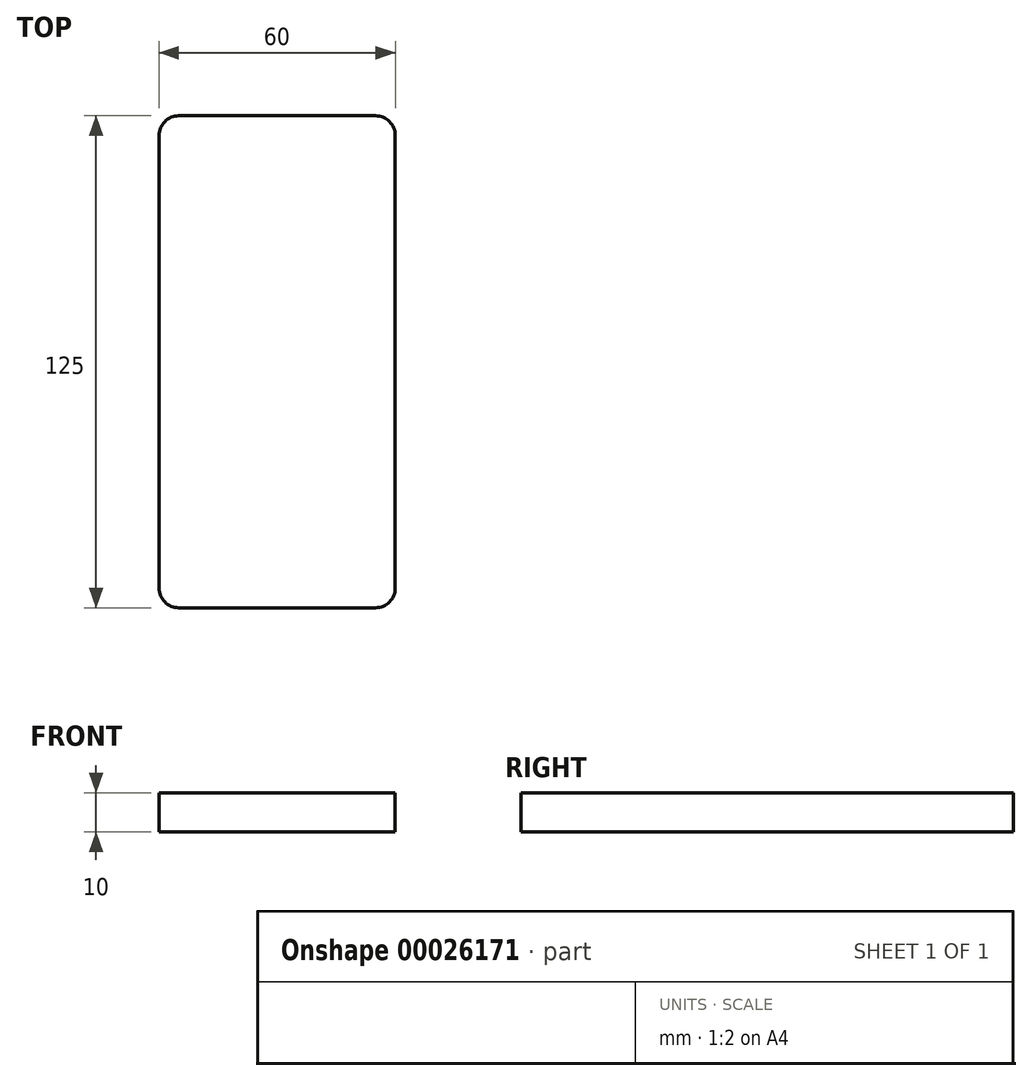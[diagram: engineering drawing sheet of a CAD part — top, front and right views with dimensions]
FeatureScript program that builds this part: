
annotation { "Feature Type Name" : "Feature", "Feature Type Description" : "" }
export const myFeature = defineFeature(function(context is Context, id is Id, definition is map)
    precondition{}
    {
        {
            var Q0;
            Q0=qCreatedBy(makeId("Top.planeOp"),FACE);
            var sketch = newSketch(context, id + "F0", { "sketchPlane" : qUnion([Q0])});
            skLineSegment(sketch, "E0.bottom", {"start": v(-32.55, -27.58) * mm, "end": v(27.45, -27.58) * mm});
            skLineSegment(sketch, "E0.top", {"start": v(-32.55, 97.42) * mm, "end": v(27.45, 97.42) * mm});
            skLineSegment(sketch, "E0.left", {"start": v(-32.55, -27.58) * mm, "end": v(-32.55, 97.42) * mm});
            skLineSegment(sketch, "E0.right", {"start": v(27.45, -27.58) * mm, "end": v(27.45, 97.42) * mm});
            skSolve(sketch);
        }
        {
            var Q0;
            Q0=makeQuery(id+"F0.imprint","IMPRINT",FACE,{"disambiguationData":[TD([[makeQuery(id+"F0.imprint","IMPRINT",EDGE,{"derivedFrom":sQuery(id+"F0.wireOp",EDGE,"E0.bottom")}),1.0]])]});
            extrude(context, id + "F1", {"entities" : qUnion([Q0]), "depth" : 10 * mm});
        }
        {
            var Q0;
            Q0=makeQuery(id+"F1.opExtrude","SWEPT_EDGE",EDGE,{"disambiguationData":[OSD([sQuery(id+"F0.wireOp",EDGE,"E0.bottom"),sQuery(id+"F0.wireOp",EDGE,"E0.left")])]});
            var Q1;
            Q1=makeQuery(id+"F1.opExtrude","SWEPT_EDGE",EDGE,{"disambiguationData":[OSD([sQuery(id+"F0.wireOp",EDGE,"E0.top"),sQuery(id+"F0.wireOp",EDGE,"E0.left")])]});
            var Q2;
            Q2=makeQuery(id+"F1.opExtrude","SWEPT_EDGE",EDGE,{"disambiguationData":[OSD([sQuery(id+"F0.wireOp",EDGE,"E0.top"),sQuery(id+"F0.wireOp",EDGE,"E0.right")])]});
            fillet(context, id + "F2", {"entities" : qUnion([Q0, Q1, Q2]), "radius" : 5 * mm, "tangentPropagation" : true, "allowEdgeOverflow" : false});
        }
        {
            var Q0;
            Q0=makeQuery(id+"F1.opExtrude","SWEPT_EDGE",EDGE,{"disambiguationData":[OSD([sQuery(id+"F0.wireOp",EDGE,"E0.bottom"),sQuery(id+"F0.wireOp",EDGE,"E0.right")])]});
            fillet(context, id + "F3", {"entities" : qUnion([Q0]), "radius" : 5 * mm, "tangentPropagation" : true, "allowEdgeOverflow" : false});
        }
        {
            var Q0;
            Q0=qCreatedBy(makeId("Front.planeOp"),FACE);
            var sketch = newSketch(context, id + "F4", { "sketchPlane" : qUnion([Q0])});
            skLineSegment(sketch, "E1.bottom", {"start": v(19.52, 6.94) * mm, "end": v(9.3, 6.94) * mm});
            skLineSegment(sketch, "E1.top", {"start": v(19.52, 3.28) * mm, "end": v(9.3, 3.28) * mm});
            skLineSegment(sketch, "E1.left", {"start": v(19.52, 6.94) * mm, "end": v(19.52, 3.28) * mm});
            skLineSegment(sketch, "E1.right", {"start": v(9.3, 6.94) * mm, "end": v(9.3, 3.28) * mm});
            skSolve(sketch);
        }
        {
            var Q0;
            Q0 = qSketchRegion(id + "F4", true);
            var Q1;
            Q1=makeQuery(id+"F1.opExtrude","SWEPT_FACE",FACE,{"disambiguationData":[OSD([sQuery(id+"F0.wireOp",EDGE,"E0.top")])]});
            extrude(context, id + "F5", {"entities" : qUnion([Q0, Q1]), "operationType" : NewBodyOperationType.ADD, "depth" : 1 * mm});
        }
        {
            var Q0;
            Q0=qCreatedBy(makeId("Front.planeOp"),FACE);
            var sketch = newSketch(context, id + "F6", { "sketchPlane" : qUnion([Q0])});
            skLineSegment(sketch, "E2.bottom", {"start": v(-51.26, -20.84) * mm, "end": v(-39.33, -20.84) * mm});
            skLineSegment(sketch, "E2.top", {"start": v(-51.26, -24.12) * mm, "end": v(-39.33, -24.12) * mm});
            skLineSegment(sketch, "E2.left", {"start": v(-51.26, -20.84) * mm, "end": v(-51.26, -24.12) * mm});
            skLineSegment(sketch, "E2.right", {"start": v(-39.33, -20.84) * mm, "end": v(-39.33, -24.12) * mm});
            skSolve(sketch);
        }
        {
            var Q0;
            Q0=sQuery(id+"F6.wireOp",EDGE,"E2.top");
            extrude(context, id + "F7", {"bodyType" : ToolBodyType.SURFACE, "surfaceEntities" : qUnion([Q0]), "depth" : 1 * mm});
        }
        {
            var Q0;
            Q0=qCreatedBy(makeId("Front.planeOp"),FACE);
            var sketch = newSketch(context, id + "F8", { "sketchPlane" : qUnion([Q0])});
            skLineSegment(sketch, "E3.bottom", {"start": v(-51.26, -20.84) * mm, "end": v(-40.59, -20.84) * mm});
            skLineSegment(sketch, "E3.top", {"start": v(-51.26, -24.75) * mm, "end": v(-40.59, -24.75) * mm});
            skLineSegment(sketch, "E3.left", {"start": v(-51.26, -20.84) * mm, "end": v(-51.26, -24.75) * mm});
            skLineSegment(sketch, "E3.right", {"start": v(-40.59, -20.84) * mm, "end": v(-40.59, -24.75) * mm});
            skSolve(sketch);
        }
        {
            var Q0;
            Q0=sQuery(id+"F8.wireOp",EDGE,"E3.bottom");
            extrude(context, id + "F9", {"bodyType" : ToolBodyType.SURFACE, "surfaceEntities" : qUnion([Q0]), "depth" : 1 * mm});
        }
    });
